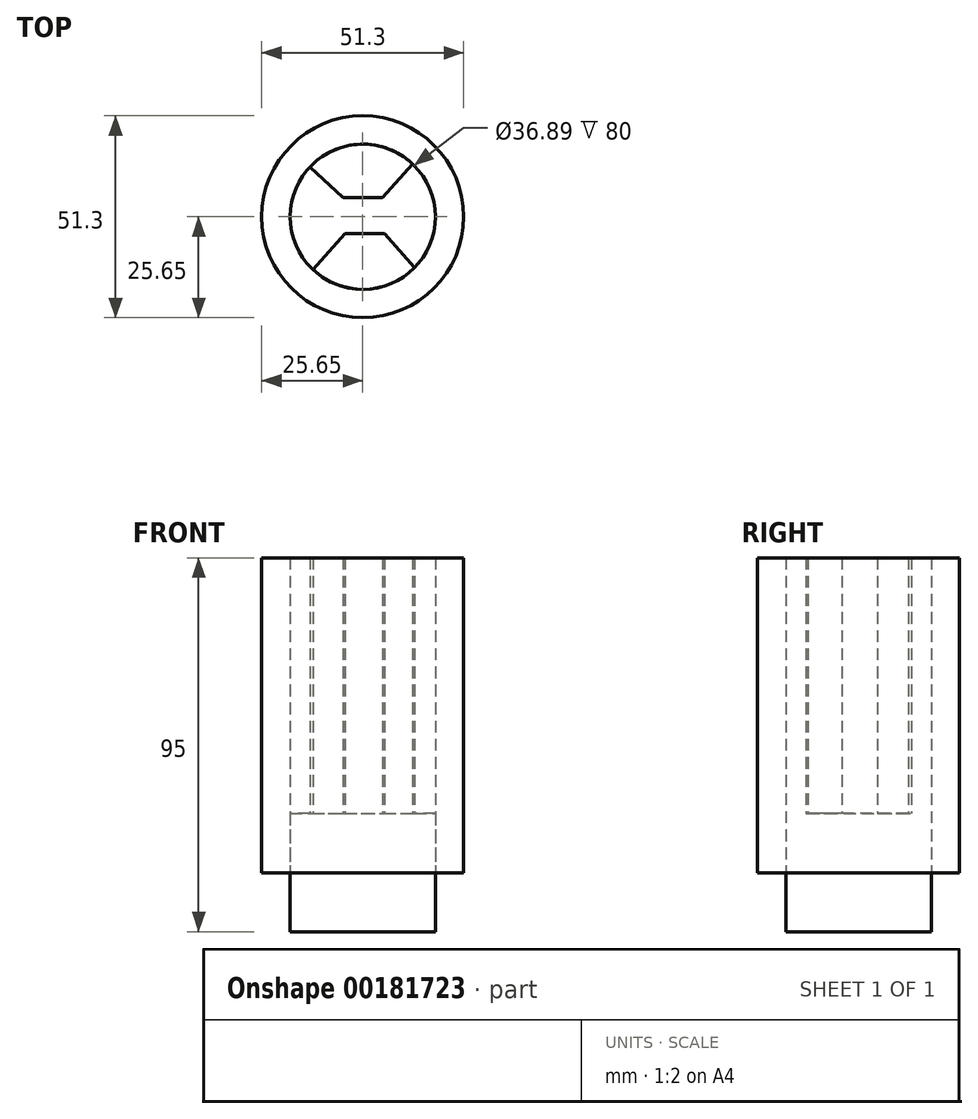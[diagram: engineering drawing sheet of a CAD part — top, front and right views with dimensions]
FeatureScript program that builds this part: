
annotation { "Feature Type Name" : "Feature", "Feature Type Description" : "" }
export const myFeature = defineFeature(function(context is Context, id is Id, definition is map)
    precondition{}
    {
        {
            var Q0;
            Q0=qCreatedBy(makeId("Top.planeOp"),FACE);
            var sketch = newSketch(context, id + "F0", { "sketchPlane" : qUnion([Q0])});
            skCircle(sketch, "E0", {"center": v(0, 0) * mm, "radius": 18.45 * mm});
            skLineSegment(sketch, "E1", {"start": v(-13.44, 12.63) * mm, "end": v(-4.98, 4.82) * mm});
            skLineSegment(sketch, "E2", {"start": v(-4.98, 4.82) * mm, "end": v(4.98, 4.82) * mm});
            skLineSegment(sketch, "E3", {"start": v(4.98, 4.82) * mm, "end": v(12.7, 13.39) * mm});
            skLineSegment(sketch, "E4.MirrorCS", {"start": v(5.5, -4.28) * mm, "end": v(13.18, -12.9) * mm});
            skLineSegment(sketch, "E5.MirrorCS", {"start": v(-12.68, -13.4) * mm, "end": v(-4.48, -4.28) * mm});
            skLineSegment(sketch, "E6.MirrorCS", {"start": v(-4.48, -4.28) * mm, "end": v(5.5, -4.28) * mm});
            skCircle(sketch, "E7", {"center": v(0, 0) * mm, "radius": 25.65 * mm});
            skSolve(sketch);
        }
        {
            var Q0;
            {var subQ0=sQuery(id+"F0.wireOp",EDGE,"E1");Q0=makeQuery(id+"F0.imprint","IMPRINT",FACE,{"disambiguationData":[TD([[makeQuery(id+"F0.imprint","IMPRINT",EDGE,{"derivedFrom":subQ0}),-1.0]])]});}
            extrude(context, id + "F1", {"entities" : qUnion([Q0]), "depth" : 15 * mm});
        }
        {
            var Q0;
            {var subQ0=sQuery(id+"F0.wireOp",EDGE,"E1");Q0=makeQuery(id+"F0.imprint","IMPRINT",FACE,{"disambiguationData":[TD([[makeQuery(id+"F0.imprint","IMPRINT",EDGE,{"derivedFrom":subQ0}),1.0]])]});}
            var Q1;
            {var subQ0=sQuery(id+"F0.wireOp",EDGE,"E1");Q1=makeQuery(id+"F0.imprint","IMPRINT",FACE,{"disambiguationData":[TD([[makeQuery(id+"F0.imprint","IMPRINT",EDGE,{"derivedFrom":subQ0}),-1.0]])]});}
            var Q2;
            {var subQ0=sQuery(id+"F0.wireOp",EDGE,"E4.MirrorCS");Q2=makeQuery(id+"F0.imprint","IMPRINT",FACE,{"disambiguationData":[TD([[makeQuery(id+"F0.imprint","IMPRINT",EDGE,{"derivedFrom":subQ0}),-1.0]])]});}
            extrude(context, id + "F2", {"entities" : qUnion([Q0, Q1, Q2]), "oppositeDirection" : true, "depth" : 15 * mm});
        }
        {
            var Q0;
            {var subQ0=sQuery(id+"F0.wireOp",EDGE,"E4.MirrorCS");Q0=makeQuery(id+"F0.imprint","IMPRINT",FACE,{"disambiguationData":[TD([[makeQuery(id+"F0.imprint","IMPRINT",EDGE,{"derivedFrom":subQ0}),-1.0]])]});}
            var Q1;
            {var subQ0=sQuery(id+"F0.wireOp",EDGE,"E1");Q1=makeQuery(id+"F0.imprint","IMPRINT",FACE,{"disambiguationData":[TD([[makeQuery(id+"F0.imprint","IMPRINT",EDGE,{"derivedFrom":subQ0}),1.0]])]});}
            extrude(context, id + "F3", {"entities" : qUnion([Q0, Q1]), "operationType" : NewBodyOperationType.ADD, "depth" : 80 * mm});
        }
        {
            var Q0;
            Q0=makeQuery(id+"F0.imprint","IMPRINT",FACE,{"disambiguationData":[TD([[makeQuery(id+"F0.imprint","IMPRINT",EDGE,{"derivedFrom":sQuery(id+"F0.wireOp",EDGE,"E7")}),1.0]])]});
            extrude(context, id + "F4", {"entities" : qUnion([Q0]), "depth" : 80 * mm});
        }
    });
